# Revit family: Shower-Showerhead-KOHLER-Venza-K-33597_1
name_source: partatom
category: Plumbing Fixtures
units: mm (PartAtom-declared; Revit-internal decimal feet)

## family parameters
Cut with Voids When Loaded = No
Host = Face
OmniClass Number = 23.31.17.00
OmniClass Title = Showers
Part Type = Normal
Room Calculation Point = No
Round Connector Dimension = Use Diameter
Shared = No

## types (3) — shared parameters
ADA Compliant = No
Assembly Code = D2010700
CW Connection = No
Cold Water Inlet = Cold Water Inlet
Date Modified = 12/12/2023
Default Elevation = 42"
Description = 1.5 GPM Single-Function Showerhead
Drain Included = No
Flow Rate = 2 GPM
HW Connection = Yes
Height = 2 3/8"
Hot Water Inlet = Tempered Water Inlet
Length = 4 1/2"
Manufacturer = Kohler Co.
Master Format 2014 = 22 42 23
Master Format 2014 Name = Residential Showers
Material = Plastic
Pressure = 45.00 psi
Product Documentation Link = https://www.us.kohler.com
Product Name = Venza
Product Page URL = http://www.us.kohler.com
URL = https://www.us.kohler.com
Vent Connection = No
Waste Connection = No
Waste Water Outlet = Waste Water Outlet
WaterSense Certified = No
Width = 4 1/2"

## per-type parameters (varying)
| type | Finish | Model | Type |
| BL-Matte Balck | Kohler-Plastic-BL-Matte_Black | K-33597-H-BL | 1 |
| BN-Vibrant Brushed Nickel | KOHLER-Plastic-BN-Vibrant_Brushed_Nickel | K-33597-H-BN | 2 |
| CP-Polished Chrome | Kohler-Plastic-CP-Polished_Chrome | K-33597-H-CP | 3 |

## geometry (parser evidence)
native form markers: Sweep x4
no freeform markers — native parametric forms only
